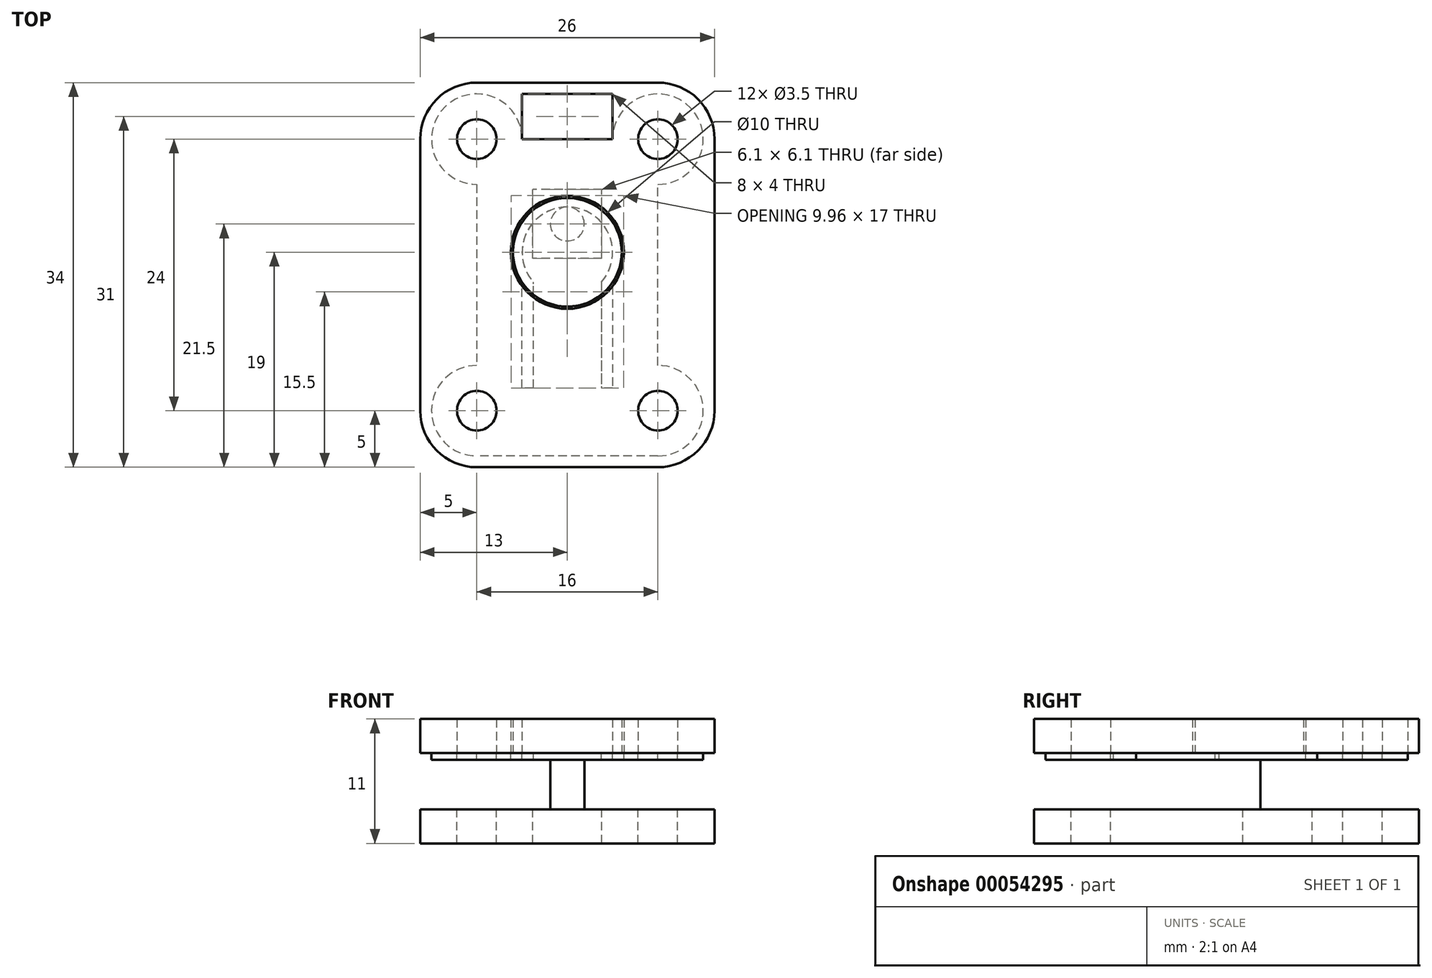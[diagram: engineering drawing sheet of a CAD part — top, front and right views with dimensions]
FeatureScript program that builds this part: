
annotation { "Feature Type Name" : "Feature", "Feature Type Description" : "" }
export const myFeature = defineFeature(function(context is Context, id is Id, definition is map)
    precondition{}
    {
        {
            var Q0;
            Q0=qCreatedBy(makeId("Top.planeOp"),FACE);
            var sketch = newSketch(context, id + "F0", { "sketchPlane" : qUnion([Q0])});
            skLineSegment(sketch, "E0.rect.bottom", {"start": v(13, 17) * mm, "end": v(-13, 17) * mm});
            skLineSegment(sketch, "E0.rect.top", {"start": v(13, -17) * mm, "end": v(-13, -17) * mm});
            skLineSegment(sketch, "E0.rect.left", {"start": v(13, 17) * mm, "end": v(13, -17) * mm});
            skLineSegment(sketch, "E0.rect.right", {"start": v(-13, 17) * mm, "end": v(-13, -17) * mm});
            skPoint(sketch, "E0.rect.middle", {"position": v(0, 0) * mm});
            skCircle(sketch, "E1", {"center": v(0, 2) * mm, "radius": 5 * mm});
            skLineSegment(sketch, "E2.rect.bottom", {"start": v(8, 12) * mm, "end": v(-8, 12) * mm, "construction": true});
            skLineSegment(sketch, "E2.rect.top", {"start": v(8, -12) * mm, "end": v(-8, -12) * mm, "construction": true});
            skLineSegment(sketch, "E2.rect.left", {"start": v(8, 12) * mm, "end": v(8, -12) * mm, "construction": true});
            skLineSegment(sketch, "E2.rect.right", {"start": v(-8, 12) * mm, "end": v(-8, -12) * mm, "construction": true});
            skLineSegment(sketch, "E3.rect.bottom", {"start": v(12, 16) * mm, "end": v(-12, 16) * mm});
            skLineSegment(sketch, "E3.rect.top", {"start": v(12, -16) * mm, "end": v(-12, -16) * mm});
            skLineSegment(sketch, "E3.rect.left", {"start": v(12, 16) * mm, "end": v(12, -16) * mm});
            skLineSegment(sketch, "E3.rect.right", {"start": v(-12, 16) * mm, "end": v(-12, -16) * mm});
            skCircle(sketch, "E4", {"center": v(-8, 12) * mm, "radius": 1.75 * mm});
            skCircle(sketch, "E5", {"center": v(8, 12) * mm, "radius": 1.75 * mm});
            skCircle(sketch, "E6", {"center": v(8, -12) * mm, "radius": 1.75 * mm});
            skCircle(sketch, "E7", {"center": v(-8, -12) * mm, "radius": 1.75 * mm});
            skCircle(sketch, "E8", {"center": v(0, 2) * mm, "radius": 4 * mm});
            skCircle(sketch, "E9", {"center": v(0, 2) * mm, "radius": 4.8 * mm});
            skLineSegment(sketch, "E10.bottom", {"start": v(-3, -10) * mm, "end": v(-4, -10) * mm});
            skLineSegment(sketch, "E10.top", {"start": v(-3, 2) * mm, "end": v(-4, 2) * mm});
            skLineSegment(sketch, "E10.left", {"start": v(-3, -10) * mm, "end": v(-3, 2) * mm});
            skLineSegment(sketch, "E10.right", {"start": v(-4, -10) * mm, "end": v(-4, 2) * mm});
            skLineSegment(sketch, "E11.bottom", {"start": v(4, 2) * mm, "end": v(3, 2) * mm});
            skLineSegment(sketch, "E11.top", {"start": v(4, -10) * mm, "end": v(3, -10) * mm});
            skLineSegment(sketch, "E11.left", {"start": v(4, 2) * mm, "end": v(4, -10) * mm});
            skLineSegment(sketch, "E11.right", {"start": v(3, 2) * mm, "end": v(3, -10) * mm});
            skCircle(sketch, "E12", {"center": v(0, 4.5) * mm, "radius": 1.5 * mm});
            skLineSegment(sketch, "E13.bottom", {"start": v(-12, 8) * mm, "end": v(-8, 8) * mm});
            skLineSegment(sketch, "E13.top", {"start": v(-12, -8) * mm, "end": v(-8, -8) * mm});
            skLineSegment(sketch, "E13.left", {"start": v(-12, 8) * mm, "end": v(-12, -8) * mm});
            skLineSegment(sketch, "E13.right", {"start": v(-8, 8) * mm, "end": v(-8, -8) * mm});
            skLineSegment(sketch, "E14.bottom", {"start": v(12, -8) * mm, "end": v(8, -8) * mm});
            skLineSegment(sketch, "E14.top", {"start": v(12, 8) * mm, "end": v(8, 8) * mm});
            skLineSegment(sketch, "E14.left", {"start": v(12, -8) * mm, "end": v(12, 8) * mm});
            skLineSegment(sketch, "E14.right", {"start": v(8, -8) * mm, "end": v(8, 8) * mm});
            skLineSegment(sketch, "E15.bottom", {"start": v(-4, 16) * mm, "end": v(4, 16) * mm});
            skLineSegment(sketch, "E15.top", {"start": v(-4, 12) * mm, "end": v(4, 12) * mm});
            skLineSegment(sketch, "E15.left", {"start": v(-4, 16) * mm, "end": v(-4, 12) * mm});
            skLineSegment(sketch, "E15.right", {"start": v(4, 16) * mm, "end": v(4, 12) * mm});
            skSolve(sketch);
        }
        {
            var Q0;
            Q0=makeQuery(id+"F0.imprint","IMPRINT",FACE,{"disambiguationData":[TD([[makeQuery(id+"F0.imprint","IMPRINT",EDGE,{"derivedFrom":sQuery(id+"F0.wireOp",EDGE,"E0.rect.bottom")}),1.0]])]});
            var Q1;
            Q1=makeQuery(id+"F0.imprint","IMPRINT",FACE,{"disambiguationData":[TD([[makeQuery(id+"F0.imprint","IMPRINT",EDGE,{"derivedFrom":sQuery(id+"F0.wireOp",EDGE,"E3.rect.bottom")}),1.0]])]});
            var Q2;
            {var subQ0=sQuery(id+"F0.wireOp",EDGE,"E10.top");Q2=makeQuery(id+"F0.imprint","IMPRINT",FACE,{"disambiguationData":[TD([[makeQuery(id+"F0.imprint","IMPRINT",EDGE,{"derivedFrom":subQ0}),-1.0]])]});}
            var Q3;
            Q3=makeQuery(id+"F0.imprint","IMPRINT",FACE,{"disambiguationData":[TD([[makeQuery(id+"F0.imprint","IMPRINT",EDGE,{"derivedFrom":sQuery(id+"F0.wireOp",EDGE,"E12")}),1.0]])]});
            var Q4;
            {var subQ0=sQuery(id+"F0.wireOp",EDGE,"E10.right");var subQ1=sQuery(id+"F0.wireOp",EDGE,"E9");var subQ2=makeQuery(id+"F0.imprint","INTERSECT",VERTEX,{"derivedFrom":[subQ1,subQ0]});Q4=makeQuery(id+"F0.imprint","IMPRINT",FACE,{"disambiguationData":[TD([[makeQuery(id+"F0.imprint","IMPRINT",EDGE,{"disambiguationData":[TD([[subQ2,1.0]])],"derivedFrom":subQ1}),1.0]])]});}
            var Q5;
            {var subQ0=sQuery(id+"F0.wireOp",EDGE,"E11.bottom");Q5=makeQuery(id+"F0.imprint","IMPRINT",FACE,{"disambiguationData":[TD([[makeQuery(id+"F0.imprint","IMPRINT",EDGE,{"derivedFrom":subQ0}),1.0]])]});}
            var Q6;
            {var subQ3=sQuery(id+"F0.wireOp",EDGE,"E11.right");var subQ5=sQuery(id+"F0.wireOp",EDGE,"E9");var subQ7=makeQuery(id+"F0.imprint","INTERSECT",VERTEX,{"derivedFrom":[subQ5,subQ3]});Q6=makeQuery(id+"F0.imprint","IMPRINT",FACE,{"disambiguationData":[TD([[makeQuery(id+"F0.imprint","IMPRINT",EDGE,{"disambiguationData":[TD([[subQ7,-1.0]])],"derivedFrom":subQ5}),1.0]])]});}
            var Q7;
            {var subQ0=sQuery(id+"F0.wireOp",EDGE,"E10.left");var subQ1=sQuery(id+"F0.wireOp",EDGE,"E8");var subQ2=makeQuery(id+"F0.imprint","INTERSECT",VERTEX,{"derivedFrom":[subQ1,subQ0]});Q7=makeQuery(id+"F0.imprint","IMPRINT",FACE,{"disambiguationData":[TD([[makeQuery(id+"F0.imprint","IMPRINT",EDGE,{"disambiguationData":[TD([[subQ2,-1.0]])],"derivedFrom":subQ1}),-1.0]])]});}
            var Q8;
            {var subQ3=sQuery(id+"F0.wireOp",EDGE,"E10.left");var subQ5=sQuery(id+"F0.wireOp",EDGE,"E9");var subQ7=makeQuery(id+"F0.imprint","INTERSECT",VERTEX,{"derivedFrom":[subQ5,subQ3]});Q8=makeQuery(id+"F0.imprint","IMPRINT",FACE,{"disambiguationData":[TD([[makeQuery(id+"F0.imprint","IMPRINT",EDGE,{"disambiguationData":[TD([[subQ7,1.0]])],"derivedFrom":subQ5}),1.0]])]});}
            var Q9;
            {var subQ0=sQuery(id+"F0.wireOp",EDGE,"E10.top");Q9=makeQuery(id+"F0.imprint","IMPRINT",FACE,{"disambiguationData":[TD([[makeQuery(id+"F0.imprint","IMPRINT",EDGE,{"derivedFrom":subQ0}),1.0]])]});}
            var Q10;
            {var subQ5=sQuery(id+"F0.wireOp",EDGE,"E10.bottom");Q10=makeQuery(id+"F0.imprint","IMPRINT",FACE,{"disambiguationData":[TD([[makeQuery(id+"F0.imprint","IMPRINT",EDGE,{"derivedFrom":subQ5}),-1.0]])]});}
            var Q11;
            {var subQ5=sQuery(id+"F0.wireOp",EDGE,"E11.top");Q11=makeQuery(id+"F0.imprint","IMPRINT",FACE,{"disambiguationData":[TD([[makeQuery(id+"F0.imprint","IMPRINT",EDGE,{"derivedFrom":subQ5}),-1.0]])]});}
            var Q12;
            Q12=makeQuery(id+"F0.imprint","IMPRINT",FACE,{"disambiguationData":[TD([[makeQuery(id+"F0.imprint","IMPRINT",EDGE,{"derivedFrom":sQuery(id+"F0.wireOp",EDGE,"E14.bottom")}),-1.0]])]});
            var Q13;
            Q13=makeQuery(id+"F0.imprint","IMPRINT",FACE,{"disambiguationData":[TD([[makeQuery(id+"F0.imprint","IMPRINT",EDGE,{"derivedFrom":sQuery(id+"F0.wireOp",EDGE,"E13.bottom")}),-1.0]])]});
            var Q14;
            Q14=makeQuery(id+"F0.imprint","IMPRINT",FACE,{"disambiguationData":[TD([[makeQuery(id+"F0.imprint","IMPRINT",EDGE,{"derivedFrom":sQuery(id+"F0.wireOp",EDGE,"E15.bottom")}),-1.0]])]});
            extrude(context, id + "F1", {"entities" : qUnion([Q0, Q1, Q2, Q3, Q4, Q5, Q6, Q7, Q8, Q9, Q10, Q11, Q12, Q13, Q14]), "depth" : 3 * mm});
        }
        {
            var Q0;
            Q0=makeQuery(id+"F0.imprint","IMPRINT",FACE,{"disambiguationData":[TD([[makeQuery(id+"F0.imprint","IMPRINT",EDGE,{"derivedFrom":sQuery(id+"F0.wireOp",EDGE,"E3.rect.bottom")}),1.0]])]});
            var Q1;
            {var subQ0=sQuery(id+"F0.wireOp",EDGE,"E10.top");Q1=makeQuery(id+"F0.imprint","IMPRINT",FACE,{"disambiguationData":[TD([[makeQuery(id+"F0.imprint","IMPRINT",EDGE,{"derivedFrom":subQ0}),-1.0]])]});}
            var Q2;
            {var subQ0=sQuery(id+"F0.wireOp",EDGE,"E10.left");var subQ1=sQuery(id+"F0.wireOp",EDGE,"E8");var subQ2=makeQuery(id+"F0.imprint","INTERSECT",VERTEX,{"derivedFrom":[subQ1,subQ0]});Q2=makeQuery(id+"F0.imprint","IMPRINT",FACE,{"disambiguationData":[TD([[makeQuery(id+"F0.imprint","IMPRINT",EDGE,{"disambiguationData":[TD([[subQ2,-1.0]])],"derivedFrom":subQ1}),-1.0]])]});}
            var Q3;
            {var subQ0=sQuery(id+"F0.wireOp",EDGE,"E10.left");var subQ1=sQuery(id+"F0.wireOp",EDGE,"E1");var subQ2=makeQuery(id+"F0.imprint","INTERSECT",VERTEX,{"derivedFrom":[subQ1,subQ0]});Q3=makeQuery(id+"F0.imprint","IMPRINT",FACE,{"disambiguationData":[TD([[makeQuery(id+"F0.imprint","IMPRINT",EDGE,{"disambiguationData":[TD([[subQ2,-1.0]])],"derivedFrom":subQ1}),1.0]])]});}
            var Q4;
            {var subQ0=sQuery(id+"F0.wireOp",EDGE,"E11.bottom");Q4=makeQuery(id+"F0.imprint","IMPRINT",FACE,{"disambiguationData":[TD([[makeQuery(id+"F0.imprint","IMPRINT",EDGE,{"derivedFrom":subQ0}),1.0]])]});}
            var Q5;
            {var subQ0=sQuery(id+"F0.wireOp",EDGE,"E10.top");Q5=makeQuery(id+"F0.imprint","IMPRINT",FACE,{"disambiguationData":[TD([[makeQuery(id+"F0.imprint","IMPRINT",EDGE,{"derivedFrom":subQ0}),1.0]])]});}
            var Q6;
            Q6=makeQuery(id+"F0.imprint","IMPRINT",FACE,{"disambiguationData":[TD([[makeQuery(id+"F0.imprint","IMPRINT",EDGE,{"derivedFrom":sQuery(id+"F0.wireOp",EDGE,"E12")}),1.0]])]});
            extrude(context, id + "F2", {"entities" : qUnion([Q0, Q1, Q2, Q3, Q4, Q5, Q6]), "oppositeDirection" : true, "depth" : 0.6 * mm});
        }
        {
            var Q0;
            Q0=makeQuery(id+"F0.imprint","IMPRINT",FACE,{"disambiguationData":[TD([[makeQuery(id+"F0.imprint","IMPRINT",EDGE,{"derivedFrom":sQuery(id+"F0.wireOp",EDGE,"E12")}),1.0]])]});
            extrude(context, id + "F3", {"entities" : qUnion([Q0]), "operationType" : NewBodyOperationType.ADD, "oppositeDirection" : true, "depth" : 5 * mm});
        }
        {
            var Q0;
            Q0=makeQuery(id+"F2.opExtrude","SWEPT_EDGE",EDGE,{"disambiguationData":[OSD([sQuery(id+"F0.wireOp",EDGE,"E3.rect.bottom"),sQuery(id+"F0.wireOp",EDGE,"E3.rect.left")])]});
            var Q1;
            Q1=makeQuery(id+"F2.opExtrude","SWEPT_EDGE",EDGE,{"disambiguationData":[OSD([sQuery(id+"F0.wireOp",EDGE,"E3.rect.bottom"),sQuery(id+"F0.wireOp",EDGE,"E3.rect.right")])]});
            var Q2;
            Q2=makeQuery(id+"F2.opExtrude","SWEPT_EDGE",EDGE,{"disambiguationData":[OSD([sQuery(id+"F0.wireOp",EDGE,"E3.rect.top"),sQuery(id+"F0.wireOp",EDGE,"E3.rect.right")])]});
            var Q3;
            Q3=makeQuery(id+"F2.opExtrude","SWEPT_EDGE",EDGE,{"disambiguationData":[OSD([sQuery(id+"F0.wireOp",EDGE,"E3.rect.top"),sQuery(id+"F0.wireOp",EDGE,"E3.rect.left")])]});
            var Q4;
            Q4=makeQuery(id+"F2.opExtrude","SWEPT_EDGE",EDGE,{"disambiguationData":[OSD([sQuery(id+"F0.wireOp",EDGE,"E3.rect.left"),sQuery(id+"F0.wireOp",EDGE,"E14.top"),sQuery(id+"F0.wireOp",EDGE,"E14.left")])]});
            var Q5;
            Q5=makeQuery(id+"F2.opExtrude","SWEPT_EDGE",EDGE,{"disambiguationData":[OSD([sQuery(id+"F0.wireOp",EDGE,"E3.rect.bottom"),sQuery(id+"F0.wireOp",EDGE,"E15.bottom"),sQuery(id+"F0.wireOp",EDGE,"E15.right")])]});
            var Q6;
            Q6=makeQuery(id+"F2.opExtrude","SWEPT_EDGE",EDGE,{"disambiguationData":[OSD([sQuery(id+"F0.wireOp",EDGE,"E3.rect.right"),sQuery(id+"F0.wireOp",EDGE,"E13.bottom"),sQuery(id+"F0.wireOp",EDGE,"E13.left")])]});
            var Q7;
            Q7=makeQuery(id+"F2.opExtrude","SWEPT_EDGE",EDGE,{"disambiguationData":[OSD([sQuery(id+"F0.wireOp",EDGE,"E3.rect.bottom"),sQuery(id+"F0.wireOp",EDGE,"E15.bottom"),sQuery(id+"F0.wireOp",EDGE,"E15.left")])]});
            var Q8;
            Q8=makeQuery(id+"F2.opExtrude","SWEPT_EDGE",EDGE,{"disambiguationData":[OSD([sQuery(id+"F0.wireOp",EDGE,"E3.rect.left"),sQuery(id+"F0.wireOp",EDGE,"E14.bottom"),sQuery(id+"F0.wireOp",EDGE,"E14.left")])]});
            var Q9;
            Q9=makeQuery(id+"F2.opExtrude","SWEPT_EDGE",EDGE,{"disambiguationData":[OSD([sQuery(id+"F0.wireOp",EDGE,"E3.rect.right"),sQuery(id+"F0.wireOp",EDGE,"E13.top"),sQuery(id+"F0.wireOp",EDGE,"E13.left")])]});
            fillet(context, id + "F4", {"entities" : qUnion([Q0, Q1, Q2, Q3, Q4, Q5, Q6, Q7, Q8, Q9]), "radius" : 4 * mm, "tangentPropagation" : true, "allowEdgeOverflow" : false});
        }
        {
            var Q0;
            Q0=makeQuery(id+"F3.opExtrude","CAP_FACE",FACE,{"disambiguationData":[OSD([sQuery(id+"F0.wireOp",EDGE,"E12")])],"isStart":false});
            var sketch = newSketch(context, id + "F5", { "sketchPlane" : qUnion([Q0])});
            skLineSegment(sketch, "E16.rect.bottom", {"start": v(3.05, -1.45) * mm, "end": v(-3.05, -1.45) * mm});
            skLineSegment(sketch, "E16.rect.top", {"start": v(3.05, -7.55) * mm, "end": v(-3.05, -7.55) * mm});
            skLineSegment(sketch, "E16.rect.left", {"start": v(3.05, -1.45) * mm, "end": v(3.05, -7.55) * mm});
            skLineSegment(sketch, "E16.rect.right", {"start": v(-3.05, -1.45) * mm, "end": v(-3.05, -7.55) * mm});
            skPoint(sketch, "E16.rect.middle", {"position": v(0, -4.5) * mm});
            skLineSegment(sketch, "E17.0.0", {"start": v(13, 17) * mm, "end": v(13, -17) * mm});
            skLineSegment(sketch, "E17.0.1", {"start": v(13, -17) * mm, "end": v(-13, -17) * mm});
            skLineSegment(sketch, "E17.0.2", {"start": v(-13, -17) * mm, "end": v(-13, 17) * mm});
            skLineSegment(sketch, "E17.0.3", {"start": v(-13, 17) * mm, "end": v(13, 17) * mm});
            skCircle(sketch, "E18.0", {"center": v(8, -12) * mm, "radius": 1.75 * mm});
            skCircle(sketch, "E19.0", {"center": v(-8, -12) * mm, "radius": 1.75 * mm});
            skCircle(sketch, "E20.0", {"center": v(-8, 12) * mm, "radius": 1.75 * mm});
            skCircle(sketch, "E21.0", {"center": v(8, 12) * mm, "radius": 1.75 * mm});
            skSolve(sketch);
        }
        {
            var Q0;
            Q0=makeQuery(id+"F5.imprint","IMPRINT",FACE,{"disambiguationData":[TD([[makeQuery(id+"F5.imprint","IMPRINT",EDGE,{"derivedFrom":sQuery(id+"F5.wireOp",EDGE,"E16.rect.bottom")}),-1.0]])]});
            extrude(context, id + "F6", {"entities" : qUnion([Q0]), "depth" : 3 * mm});
        }
        {
            var Q0;
            Q0=makeQuery(id+"F6.opExtrude","SWEPT_EDGE",EDGE,{"disambiguationData":[OSD([sQuery(id+"F5.wireOp",EDGE,"E17.0.1"),sQuery(id+"F5.wireOp",EDGE,"E17.0.2")])]});
            var Q1;
            Q1=makeQuery(id+"F1.opExtrude","SWEPT_EDGE",EDGE,{"disambiguationData":[OSD([sQuery(id+"F0.wireOp",EDGE,"E0.rect.bottom"),sQuery(id+"F0.wireOp",EDGE,"E0.rect.right")])]});
            var Q2;
            Q2=makeQuery(id+"F6.opExtrude","SWEPT_EDGE",EDGE,{"disambiguationData":[OSD([sQuery(id+"F5.wireOp",EDGE,"E17.0.2"),sQuery(id+"F5.wireOp",EDGE,"E17.0.3")])]});
            var Q3;
            Q3=makeQuery(id+"F1.opExtrude","SWEPT_EDGE",EDGE,{"disambiguationData":[OSD([sQuery(id+"F0.wireOp",EDGE,"E0.rect.top"),sQuery(id+"F0.wireOp",EDGE,"E0.rect.right")])]});
            var Q4;
            Q4=makeQuery(id+"F6.opExtrude","SWEPT_EDGE",EDGE,{"disambiguationData":[OSD([sQuery(id+"F5.wireOp",EDGE,"E17.0.0"),sQuery(id+"F5.wireOp",EDGE,"E17.0.3")])]});
            var Q5;
            Q5=makeQuery(id+"F1.opExtrude","SWEPT_EDGE",EDGE,{"disambiguationData":[OSD([sQuery(id+"F0.wireOp",EDGE,"E0.rect.top"),sQuery(id+"F0.wireOp",EDGE,"E0.rect.left")])]});
            var Q6;
            Q6=makeQuery(id+"F6.opExtrude","SWEPT_EDGE",EDGE,{"disambiguationData":[OSD([sQuery(id+"F5.wireOp",EDGE,"E17.0.0"),sQuery(id+"F5.wireOp",EDGE,"E17.0.1")])]});
            var Q7;
            Q7=makeQuery(id+"F1.opExtrude","SWEPT_EDGE",EDGE,{"disambiguationData":[OSD([sQuery(id+"F0.wireOp",EDGE,"E0.rect.bottom"),sQuery(id+"F0.wireOp",EDGE,"E0.rect.left")])]});
            fillet(context, id + "F7", {"entities" : qUnion([Q0, Q1, Q2, Q3, Q4, Q5, Q6, Q7]), "radius" : 5 * mm, "tangentPropagation" : true, "allowEdgeOverflow" : false});
        }
    });
